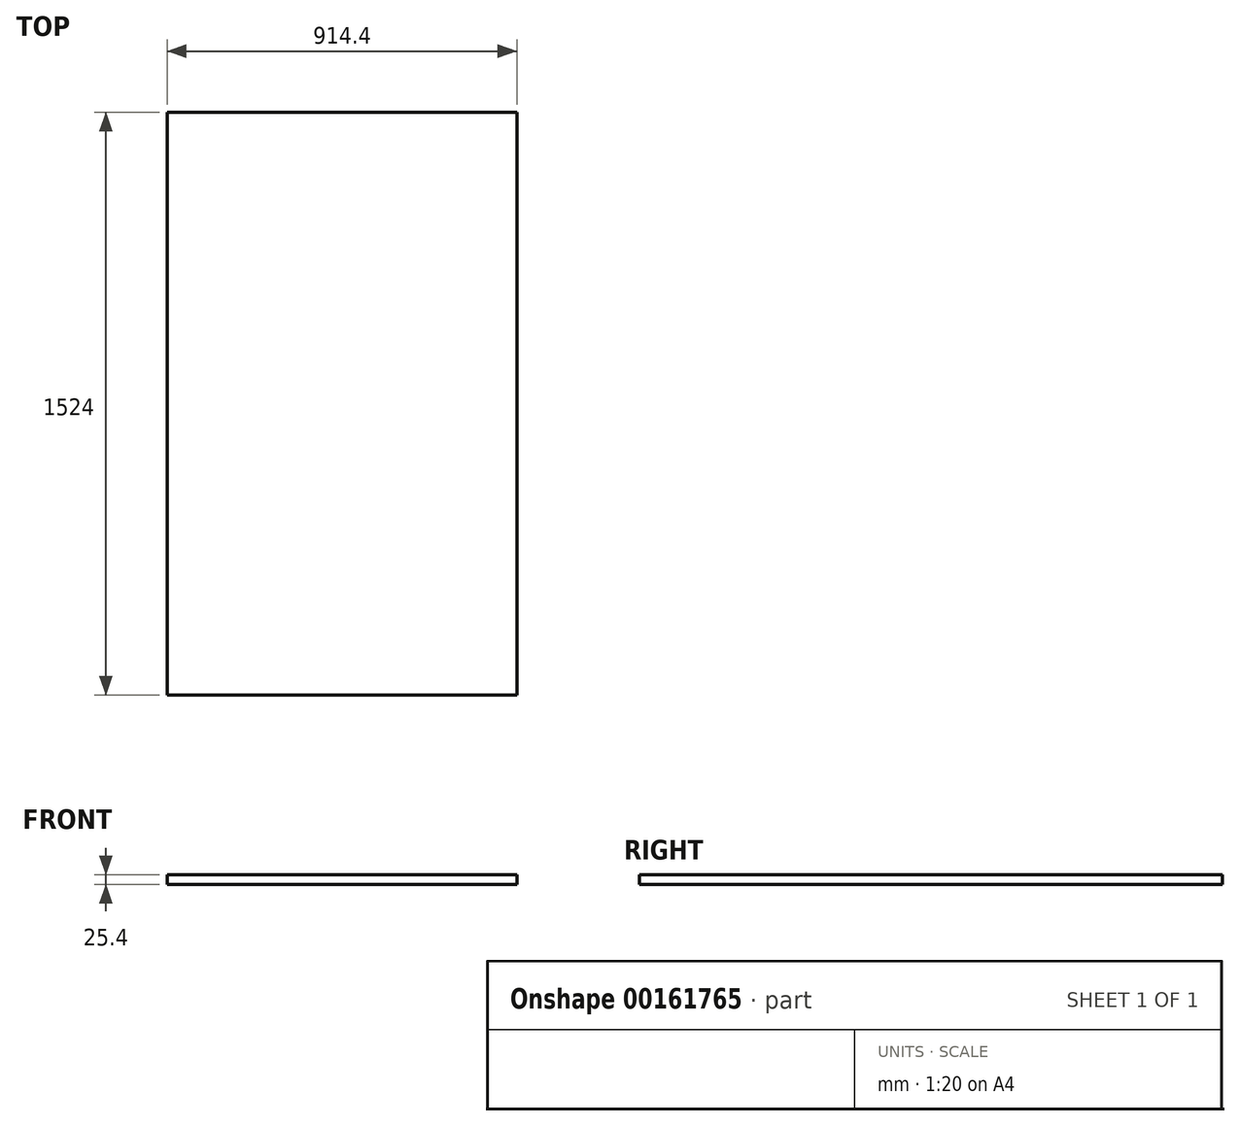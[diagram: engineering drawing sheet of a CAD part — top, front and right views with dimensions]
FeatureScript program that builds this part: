
annotation { "Feature Type Name" : "Feature", "Feature Type Description" : "" }
export const myFeature = defineFeature(function(context is Context, id is Id, definition is map)
    precondition{}
    {
        {
            var Q0;
            Q0=qCreatedBy(makeId("Top.planeOp"),FACE);
            var sketch = newSketch(context, id + "F0", { "sketchPlane" : qUnion([Q0])});
            skLineSegment(sketch, "E0.bottom", {"start": v(-459.5, -707.39) * mm, "end": v(454.9, -707.39) * mm});
            skLineSegment(sketch, "E0.top", {"start": v(-459.5, 816.61) * mm, "end": v(454.9, 816.61) * mm});
            skLineSegment(sketch, "E0.left", {"start": v(-459.5, -707.39) * mm, "end": v(-459.5, 816.61) * mm});
            skLineSegment(sketch, "E0.right", {"start": v(454.9, -707.39) * mm, "end": v(454.9, 816.61) * mm});
            skSolve(sketch);
        }
        {
            var Q0;
            Q0=makeQuery(id+"F0.imprint","IMPRINT",FACE,{"disambiguationData":[TD([[makeQuery(id+"F0.imprint","IMPRINT",EDGE,{"derivedFrom":sQuery(id+"F0.wireOp",EDGE,"E0.bottom")}),1.0]])]});
            extrude(context, id + "F1", {"entities" : qUnion([Q0]), "depth" : 25.4 * mm});
        }
    });
